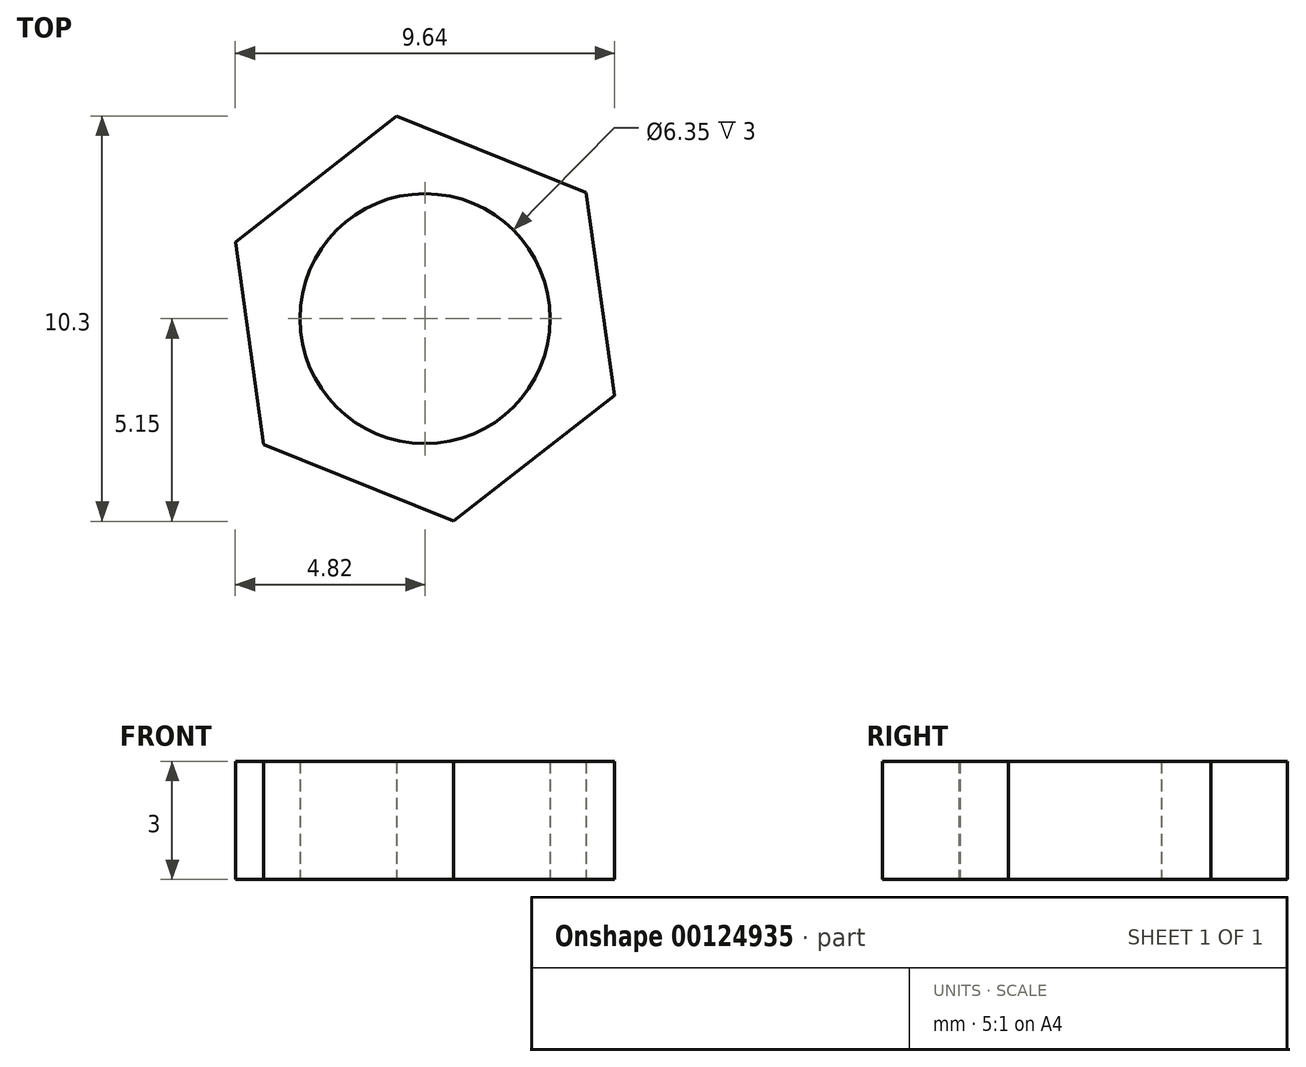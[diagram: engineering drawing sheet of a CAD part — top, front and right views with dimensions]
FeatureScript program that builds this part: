
annotation { "Feature Type Name" : "Feature", "Feature Type Description" : "" }
export const myFeature = defineFeature(function(context is Context, id is Id, definition is map)
    precondition{}
    {
        {
            var Q0;
            Q0=qCreatedBy(makeId("Top.planeOp"),FACE);
            var sketch = newSketch(context, id + "F0", { "sketchPlane" : qUnion([Q0])});
            skCircle(sketch, "E0", {"center": v(0, 0) * mm, "radius": 3.17 * mm});
            skCircle(sketch, "E1.cCircle", {"center": v(0, 0) * mm, "radius": 4.5 * mm, "construction": true});
            skLineSegment(sketch, "E1.0", {"start": v(4.82, -1.95) * mm, "end": v(0.72, -5.15) * mm});
            skLineSegment(sketch, "E1.1", {"start": v(0.72, -5.15) * mm, "end": v(-4.1, -3.2) * mm});
            skLineSegment(sketch, "E1.2", {"start": v(-4.1, -3.2) * mm, "end": v(-4.82, 1.95) * mm});
            skLineSegment(sketch, "E1.3", {"start": v(-4.82, 1.95) * mm, "end": v(-0.72, 5.15) * mm});
            skLineSegment(sketch, "E1.4", {"start": v(-0.72, 5.15) * mm, "end": v(4.1, 3.2) * mm});
            skLineSegment(sketch, "E1.5", {"start": v(4.1, 3.2) * mm, "end": v(4.82, -1.95) * mm});
            skPoint(sketch, "E1.0.midPoint", {"position": v(2.77, -3.55) * mm});
            skSolve(sketch);
        }
        {
            var Q0;
            Q0=makeQuery(id+"F0.imprint","IMPRINT",FACE,{"disambiguationData":[TD([[makeQuery(id+"F0.imprint","IMPRINT",EDGE,{"derivedFrom":sQuery(id+"F0.wireOp",EDGE,"E0")}),-1.0]])]});
            extrude(context, id + "F1", {"entities" : qUnion([Q0]), "depth" : 3 * mm});
        }
    });
